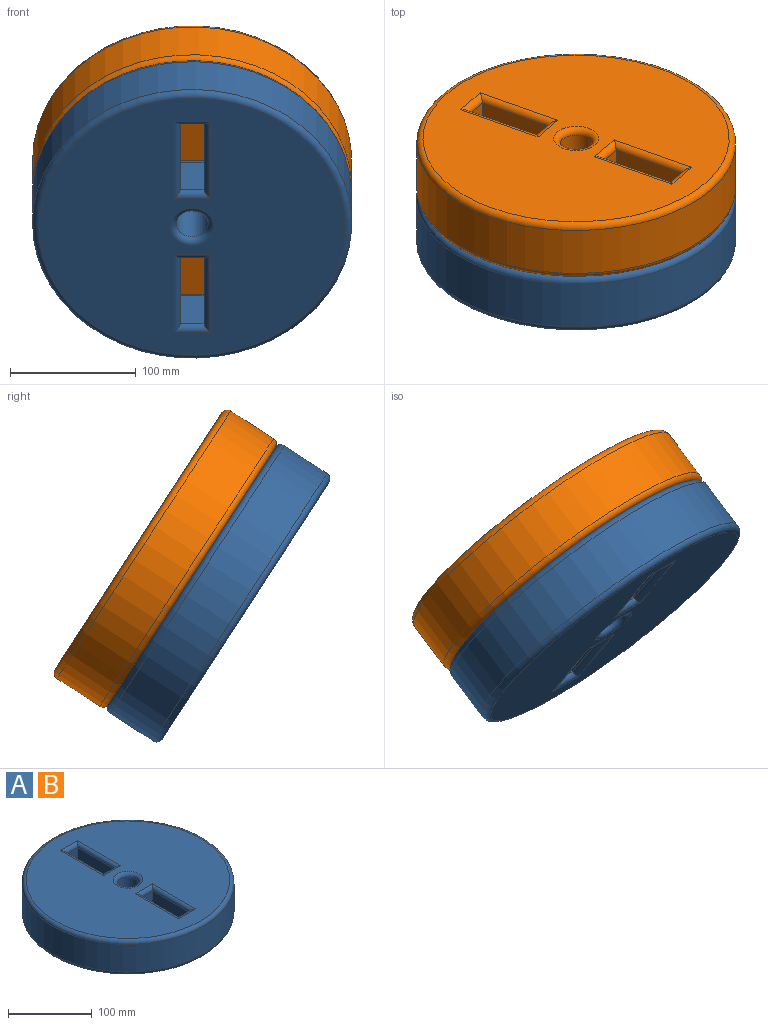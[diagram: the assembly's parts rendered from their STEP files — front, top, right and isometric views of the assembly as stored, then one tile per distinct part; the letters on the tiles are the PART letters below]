
ASSEMBLY  parts=2 mates=1
PART A: 32 faces, bbox 274.9x274.9x50.8 mm
  f0: plane 243.84x243.84mm, normal (0,0,1), area 41401.8mm2, adj f13,f22,f23,f24,f25,f26,f27,f28
  f1: plane 243.84x243.84mm, normal (0,0,-1), area 41401.8mm2, adj f12,f14,f15,f16,f17,f18,f19,f20
  f2: cylinder r=127mm len=254mm, axis (0,0,-1), area 32429.3mm2, adj f30,f31
  f3: plane 63.5x40.64mm, normal (-1,0,0), area 2580.6mm2, adj f4,f6,f21,f22
  f4: plane 40.64x19.05mm, normal (0,-1,0), area 774.2mm2, adj f3,f5,f19,f24
  f5: plane 63.5x40.64mm, normal (1,0,0), area 2580.6mm2, adj f4,f6,f18,f25
  f6: plane 40.64x19.05mm, normal (0,1,0), area 774.2mm2, adj f3,f5,f20,f23
  f7: plane 63.5x40.64mm, normal (-1,0,0), area 2580.6mm2, adj f8,f10,f17,f27
  f8: plane 40.64x19.05mm, normal (0,-1,0), area 774.2mm2, adj f7,f9,f16,f29
  f9: plane 63.5x40.64mm, normal (1,0,0), area 2580.6mm2, adj f8,f10,f14,f28
  f10: plane 40.64x19.05mm, normal (0,1,0), area 774.2mm2, adj f7,f9,f15,f26
  f11: cylinder r=12.7mm len=40.64mm, axis (0,0,1), area 3242.9mm2, adj f12,f13
  f12: torus R=17.78mm, axis (0,0,-1), area 729.3mm2, adj f1,f11
  f13: torus R=17.78mm, axis (0,0,-1), area 729.3mm2, adj f0,f11
  f14: cylinder r=5.08mm len=73.66mm, axis (0,-1,0), area 536.2mm2, adj f1,f9,f15,f16
  f15: cylinder r=5.08mm len=29.21mm, axis (1,0,0), area 181.5mm2, adj f1,f10,f14,f17
  f16: cylinder r=5.08mm len=29.21mm, axis (-1,0,0), area 181.5mm2, adj f1,f8,f14,f17
  f17: cylinder r=5.08mm len=73.66mm, axis (0,1,0), area 536.2mm2, adj f1,f7,f15,f16
  f18: cylinder r=5.08mm len=73.66mm, axis (0,-1,0), area 536.2mm2, adj f1,f5,f19,f20
  f19: cylinder r=5.08mm len=29.21mm, axis (-1,0,0), area 181.5mm2, adj f1,f4,f18,f21
  f20: cylinder r=5.08mm len=29.21mm, axis (1,0,0), area 181.5mm2, adj f1,f6,f18,f21
  f21: cylinder r=5.08mm len=73.66mm, axis (0,1,0), area 536.2mm2, adj f1,f3,f19,f20
  f22: cylinder r=5.08mm len=73.66mm, axis (0,1,0), area 536.2mm2, adj f0,f3,f23,f24
  f23: cylinder r=5.08mm len=29.21mm, axis (1,0,0), area 181.5mm2, adj f0,f6,f22,f25
  f24: cylinder r=5.08mm len=29.21mm, axis (-1,0,0), area 181.5mm2, adj f0,f4,f22,f25
  f25: cylinder r=5.08mm len=73.66mm, axis (0,-1,0), area 536.2mm2, adj f0,f5,f23,f24
  f26: cylinder r=5.08mm len=29.21mm, axis (1,0,0), area 181.5mm2, adj f0,f10,f27,f28
  f27: cylinder r=5.08mm len=73.66mm, axis (0,1,0), area 536.2mm2, adj f0,f7,f26,f29
  f28: cylinder r=5.08mm len=73.66mm, axis (0,-1,0), area 536.2mm2, adj f0,f9,f26,f29
  f29: cylinder r=5.08mm len=29.21mm, axis (-1,0,0), area 181.5mm2, adj f0,f8,f27,f28
  f30: torus R=121.92mm, axis (0,0,-1), area 6274.9mm2, adj f1,f2
  f31: torus R=121.92mm, axis (0,0,-1), area 6274.9mm2, adj f0,f2
PART B: same geometry as A
PLACE A rot(axis=(-1,0,0),57deg) t=(379.29,168.82,59.49)mm fixed
PLACE B rot(axis=(0.85,0.46,-0.25),130.5deg) t=(379.29,254,114.87)mm
MATE revolute B.f2 <-> A.f2  axis (0,-0.84,-0.55) through (379.29,211.41,87.18)mm
